# Revit family: Accessory-Flush_Actuator_Plate-KOHLER-Summon-K-24147T_1
name_source: partatom
category: Specialty Equipment
units: mm (PartAtom-declared; Revit-internal decimal feet)

## family parameters
Cut with Voids When Loaded = No
Host = Face
OmniClass Number = 23.31.25.00
OmniClass Title = Toilet and Bath Specialties
Part Type = Normal
Room Calculation Point = No
Round Connector Dimension = Use Diameter
Shared = No

## types (1)
- 7-Black Black
    ADA Compliant = No
    Apparent Load = 8 VA
    Assembly Code = C1030200
    Date Modified = 08/04/2022
    Default Elevation = 42"
    Description = Sensor Faceplate AC with Music
    Electrical Connector = Yes
    Electrical Note = One dedicated Circuit Required
    Finish = Kohler-Glass-7-Black_Black
    Height = 6 5/16"
    Length = 8 7/8"
    Manufacturer = Kohler Co.
    Master Format 2014 = 10 28 00
    Master Format 2014 Name = Toilet, Bath, and Laundry Accessories
    Material = Glass
    Model = K-24147T-7
    Product Name = Summon
    Type = 1
    URL = http://www.kohler.com.cn
    Voltage = 220 V
    WaterSense Certified = No
    Width = 1/8"

## geometry (parser evidence)
native form markers: Sweep x4
no freeform markers — native parametric forms only
